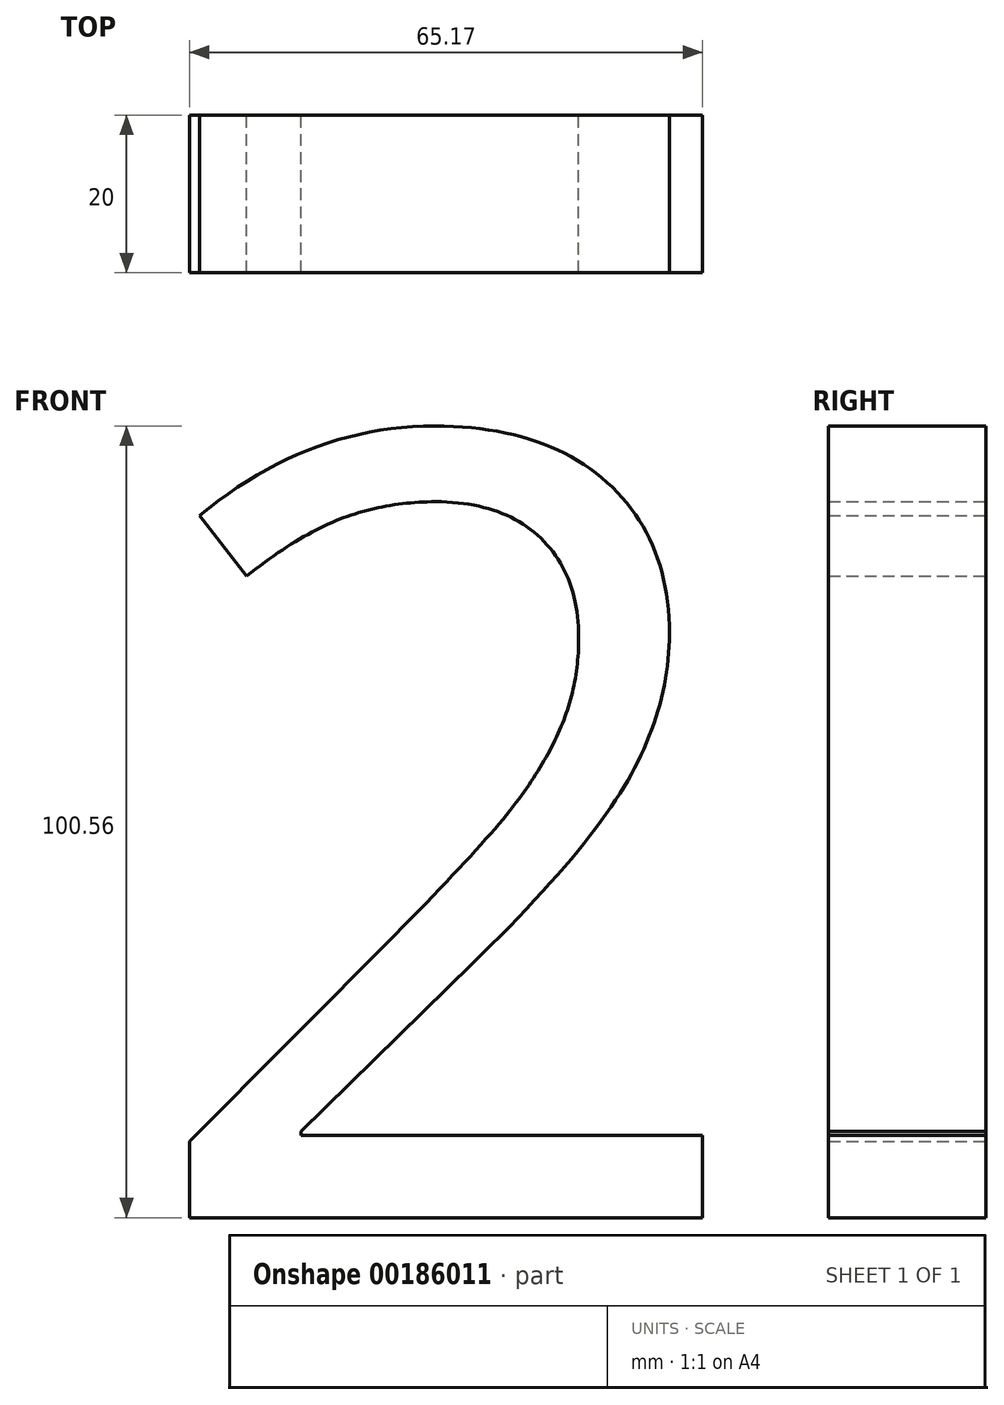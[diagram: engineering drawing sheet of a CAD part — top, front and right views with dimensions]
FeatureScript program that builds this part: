
annotation { "Feature Type Name" : "Feature", "Feature Type Description" : "" }
export const myFeature = defineFeature(function(context is Context, id is Id, definition is map)
    precondition{}
    {
        {
            var Q0;
            Q0=qCreatedBy(makeId("Front.planeOp"),FACE);
            var sketch = newSketch(context, id + "F0", { "sketchPlane" : qUnion([Q0])});
            skText(sketch, "E0", { "text": "2", "fontName": "OpenSans-Regular.ttf"});
            const initialGuessF0  = {"E0": [-0.04048, 0, 1, 0, 0.1]};
            skSetInitialGuess(sketch, initialGuessF0);
            skSolve(sketch);
        }
        {
            var Q0;
            Q0=makeQuery(id+"F0.imprint","IMPRINT",FACE,{"disambiguationData":[TD([[makeQuery(id+"F0.imprint","IMPRINT",EDGE,{"derivedFrom":sQuery(id+"F0.wireOp",EDGE,"E0.sketch_text.stroke-0")}),-1.0]])]});
            extrude(context, id + "F1", {"entities" : qUnion([Q0]), "depth" : 10 * mm, "hasSecondDirection" : true, "secondDirectionOppositeDirection" : true, "secondDirectionDepth" : 10 * mm});
        }
    });
